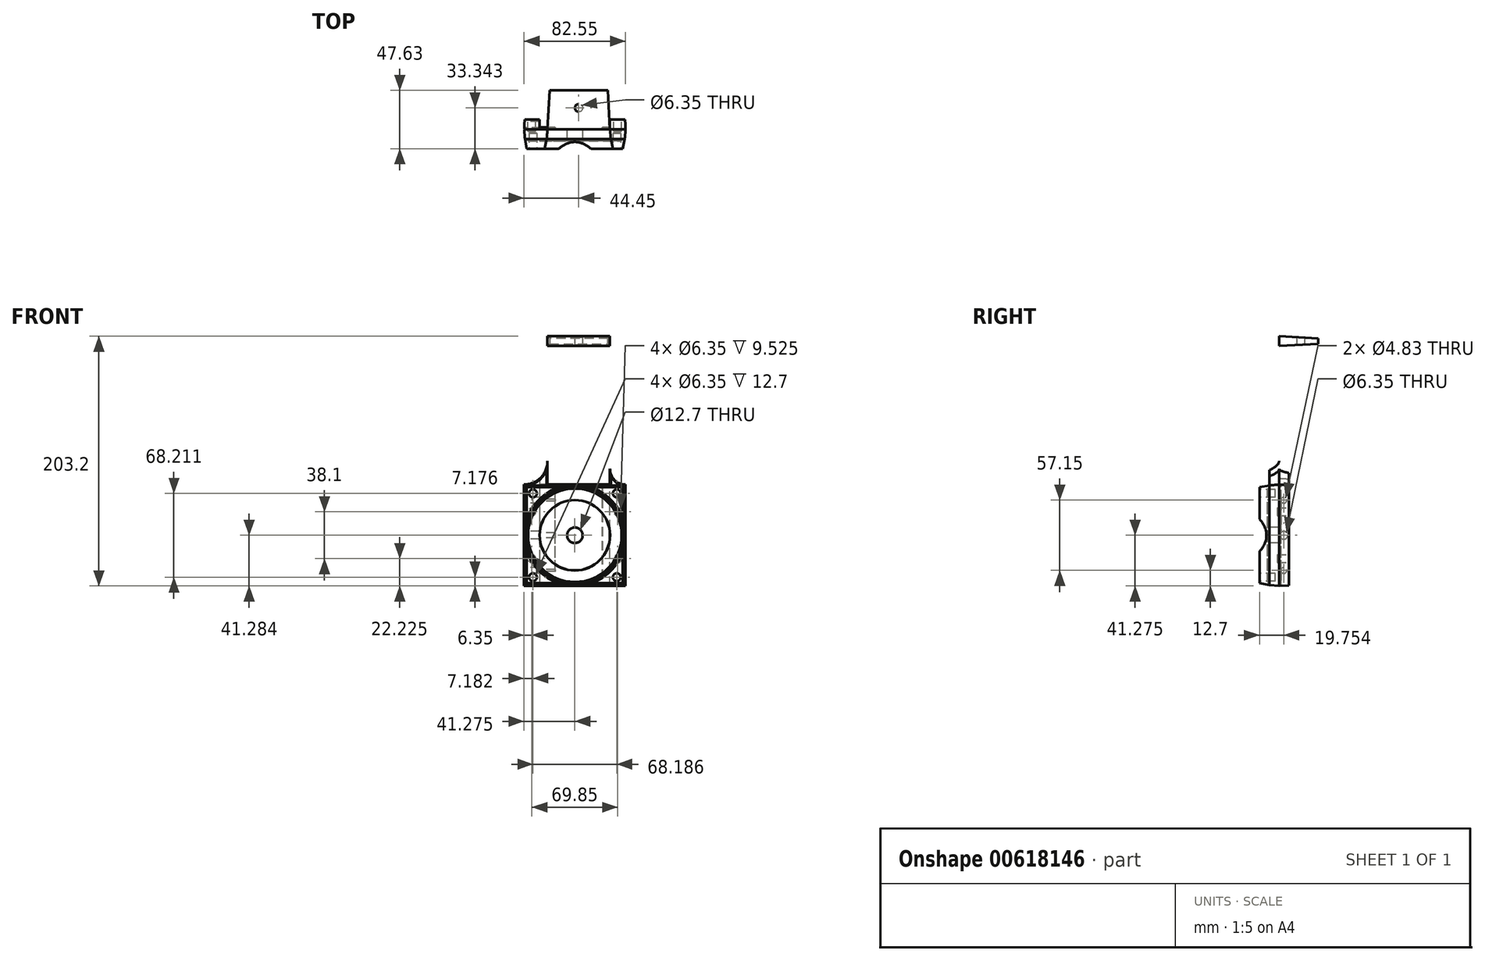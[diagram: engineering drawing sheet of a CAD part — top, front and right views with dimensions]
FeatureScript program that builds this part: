
annotation { "Feature Type Name" : "Feature", "Feature Type Description" : "" }
export const myFeature = defineFeature(function(context is Context, id is Id, definition is map)
    precondition{}
    {
        {
            var Q0;
            Q0=qCreatedBy(makeId("Front.planeOp"),FACE);
            var sketch = newSketch(context, id + "F0", { "sketchPlane" : qUnion([Q0])});
            skLineSegment(sketch, "E0.bottom", {"start": v(0, 0) * mm, "end": v(82.55, 0) * mm});
            skLineSegment(sketch, "E0.top", {"start": v(0, 82.55) * mm, "end": v(82.55, 82.55) * mm});
            skLineSegment(sketch, "E0.left", {"start": v(0, 0) * mm, "end": v(0, 82.55) * mm});
            skLineSegment(sketch, "E0.right", {"start": v(82.55, 0) * mm, "end": v(82.55, 82.55) * mm});
            skLineSegment(sketch, "E1.bottom", {"start": v(19.05, 82.55) * mm, "end": v(69.85, 82.55) * mm});
            skLineSegment(sketch, "E1.top", {"start": v(19.05, 203.2) * mm, "end": v(69.85, 203.2) * mm});
            skLineSegment(sketch, "E1.left", {"start": v(19.05, 82.55) * mm, "end": v(19.05, 203.2) * mm});
            skLineSegment(sketch, "E1.right", {"start": v(69.85, 82.55) * mm, "end": v(69.85, 203.2) * mm});
            skCircle(sketch, "E2", {"center": v(82.55, 95.25) * mm, "radius": 12.7 * mm});
            skCircle(sketch, "E3", {"center": v(0, 101.6) * mm, "radius": 19.05 * mm});
            skSolve(sketch);
        }
        {
            var Q0;
            {var subQ3=sQuery(id+"F0.wireOp",EDGE,"E1.bottom");Q0=makeQuery(id+"F0.imprint","IMPRINT",FACE,{"disambiguationData":[TD([[makeQuery(id+"F0.imprint","IMPRINT",EDGE,{"derivedFrom":subQ3}),1.0]])]});}
            var Q1;
            Q1=makeQuery(id+"F0.imprint","IMPRINT",FACE,{"disambiguationData":[TD([[makeQuery(id+"F0.imprint","IMPRINT",EDGE,{"derivedFrom":sQuery(id+"F0.wireOp",EDGE,"E0.bottom")}),1.0]])]});
            var Q2;
            {var subQ0=sQuery(id+"F0.wireOp",EDGE,"E2");var subQ3=sQuery(id+"F0.wireOp",EDGE,"E1.right");var subQ5=makeQuery(id+"F0.imprint","INTERSECT",VERTEX,{"derivedFrom":[subQ3,subQ0]});Q2=makeQuery(id+"F0.imprint","IMPRINT",FACE,{"disambiguationData":[TD([[makeQuery(id+"F0.imprint","IMPRINT",EDGE,{"disambiguationData":[TD([[subQ5,1.0]])],"derivedFrom":subQ3}),-1.0]])]});}
            var Q3;
            {var subQ0=sQuery(id+"F0.wireOp",EDGE,"E3");var subQ3=sQuery(id+"F0.wireOp",EDGE,"E1.left");var subQ5=makeQuery(id+"F0.imprint","INTERSECT",VERTEX,{"derivedFrom":[subQ3,subQ0]});Q3=makeQuery(id+"F0.imprint","IMPRINT",FACE,{"disambiguationData":[TD([[makeQuery(id+"F0.imprint","IMPRINT",EDGE,{"disambiguationData":[TD([[subQ5,1.0]])],"derivedFrom":subQ3}),1.0]])]});}
            extrude(context, id + "F1", {"entities" : qUnion([Q0, Q1, Q2, Q3]), "depth" : 7.94 * mm, "hasDraft" : true, "draftAngle" : 5 * degree, "draftPullDirection" : true});
        }
        {
            var Q0;
            Q0=makeQuery(id+"F1.opExtrude","CAP_FACE",FACE,{"disambiguationData":[OSD([sQuery(id+"F0.wireOp",EDGE,"E0.bottom"),sQuery(id+"F0.wireOp",EDGE,"E0.top"),sQuery(id+"F0.wireOp",EDGE,"E0.left"),sQuery(id+"F0.wireOp",EDGE,"E0.right"),sQuery(id+"F0.wireOp",EDGE,"E1.top"),sQuery(id+"F0.wireOp",EDGE,"E1.left"),sQuery(id+"F0.wireOp",EDGE,"E1.right")])],"isStart":true});
            var sketch = newSketch(context, id + "F2", { "sketchPlane" : qUnion([Q0])});
            skLineSegment(sketch, "E4.0", {"start": v(-19.05, 203.2) * mm, "end": v(-69.85, 203.2) * mm});
            skLineSegment(sketch, "E5", {"start": v(-69.85, 203.2) * mm, "end": v(-69.85, 195.26) * mm});
            skLineSegment(sketch, "E6", {"start": v(-69.85, 195.26) * mm, "end": v(-19.05, 195.26) * mm});
            skLineSegment(sketch, "E7", {"start": v(-19.05, 195.26) * mm, "end": v(-19.05, 203.2) * mm});
            skSolve(sketch);
        }
        {
            var Q0;
            Q0=makeQuery(id+"F2.imprint","IMPRINT",FACE,{"disambiguationData":[TD([[makeQuery(id+"F2.imprint","IMPRINT",EDGE,{"derivedFrom":sQuery(id+"F2.wireOp",EDGE,"E4.0")}),1.0]])]});
            extrude(context, id + "F3", {"entities" : qUnion([Q0]), "operationType" : NewBodyOperationType.ADD, "depth" : 31.75 * mm, "hasDraft" : true, "draftAngle" : 3 * degree, "draftPullDirection" : true});
        }
        {
            var Q0;
            Q0=makeQuery(id+"F1.opExtrude","CAP_FACE",FACE,{"disambiguationData":[OSD([sQuery(id+"F0.wireOp",EDGE,"E0.bottom"),sQuery(id+"F0.wireOp",EDGE,"E0.left"),sQuery(id+"F0.wireOp",EDGE,"E0.right"),sQuery(id+"F0.wireOp",EDGE,"E1.top"),sQuery(id+"F0.wireOp",EDGE,"E1.left"),sQuery(id+"F0.wireOp",EDGE,"E1.right"),sQuery(id+"F0.wireOp",EDGE,"E2"),sQuery(id+"F0.wireOp",EDGE,"E3")])],"isStart":true});
            var sketch = newSketch(context, id + "F4", { "sketchPlane" : qUnion([Q0])});
            skLineSegment(sketch, "E8.bottom", {"start": v(-82.55, 82.55) * mm, "end": v(-69.85, 82.55) * mm});
            skLineSegment(sketch, "E8.top", {"start": v(-82.55, 0) * mm, "end": v(-69.85, 0) * mm});
            skLineSegment(sketch, "E8.left", {"start": v(-82.55, 82.55) * mm, "end": v(-82.55, 0) * mm});
            skLineSegment(sketch, "E8.right", {"start": v(-69.85, 95.25) * mm, "end": v(-69.85, 0) * mm});
            skLineSegment(sketch, "E9.bottom", {"start": v(0, 82.55) * mm, "end": v(-12.7, 82.55) * mm});
            skLineSegment(sketch, "E9.top", {"start": v(0, 0) * mm, "end": v(-12.7, 0) * mm});
            skLineSegment(sketch, "E9.left", {"start": v(0, 82.55) * mm, "end": v(0, 0) * mm});
            skLineSegment(sketch, "E9.right", {"start": v(-12.7, 87.4) * mm, "end": v(-12.7, 0) * mm});
            skArc(sketch, "E10.0", {"start": v(-69.85, 95.25) * mm, "mid": v(-73.57, 86.27) * mm, "end": v(-82.55, 82.55) * mm});
            skArc(sketch, "E11.0", {"start": v(0, 82.55) * mm, "mid": v(-13.47, 88.13) * mm, "end": v(-19.05, 101.6) * mm});
            skSolve(sketch);
        }
        {
            var Q0;
            Q0=qSketchRegion(id+"F4",true);
            extrude(context, id + "F5", {"entities" : qUnion([Q0]), "operationType" : NewBodyOperationType.ADD, "depth" : 7.94 * mm});
        }
        {
            var Q0;
            Q0=makeQuery(id+"F1.opExtrude","CAP_FACE",FACE,{"disambiguationData":[OSD([sQuery(id+"F0.wireOp",EDGE,"E0.bottom"),sQuery(id+"F0.wireOp",EDGE,"E0.left"),sQuery(id+"F0.wireOp",EDGE,"E0.right"),sQuery(id+"F0.wireOp",EDGE,"E1.top"),sQuery(id+"F0.wireOp",EDGE,"E1.left"),sQuery(id+"F0.wireOp",EDGE,"E1.right"),sQuery(id+"F0.wireOp",EDGE,"E2"),sQuery(id+"F0.wireOp",EDGE,"E3")])],"isStart":true});
            var sketch = newSketch(context, id + "F6", { "sketchPlane" : qUnion([Q0])});
            skLineSegment(sketch, "E12.0.0", {"start": v(-12.7, 0) * mm, "end": v(-12.7, 87.4) * mm});
            skArc(sketch, "E12.0.1", {"start": v(-12.7, 87.4) * mm, "mid": v(-17.4, 93.82) * mm, "end": v(-19.05, 101.6) * mm});
            skLineSegment(sketch, "E12.0.2", {"start": v(-19.05, 101.6) * mm, "end": v(-19.05, 195.26) * mm});
            skLineSegment(sketch, "E12.0.3", {"start": v(-69.85, 195.26) * mm, "end": v(-19.05, 195.26) * mm});
            skLineSegment(sketch, "E12.0.4", {"start": v(-69.85, 95.25) * mm, "end": v(-69.85, 195.26) * mm});
            skLineSegment(sketch, "E12.0.5", {"start": v(-69.85, 95.25) * mm, "end": v(-69.85, 0) * mm});
            skLineSegment(sketch, "E12.0.6", {"start": v(-12.7, 0) * mm, "end": v(-69.85, 0) * mm});
            skLineSegment(sketch, "E13.0.0", {"start": v(0, 0) * mm, "end": v(0, 82.55) * mm});
            skArc(sketch, "E13.0.1", {"start": v(0, 82.55) * mm, "mid": v(-6.8, 83.8) * mm, "end": v(-12.7, 87.4) * mm});
            skLineSegment(sketch, "E13.0.2", {"start": v(-12.7, 87.4) * mm, "end": v(-12.7, 0) * mm});
            skLineSegment(sketch, "E13.0.3", {"start": v(0, 0) * mm, "end": v(-12.7, 0) * mm});
            skLineSegment(sketch, "E14.0.0", {"start": v(-69.85, 0) * mm, "end": v(-69.85, 95.25) * mm});
            skArc(sketch, "E14.0.1", {"start": v(-69.85, 95.25) * mm, "mid": v(-73.57, 86.27) * mm, "end": v(-82.55, 82.55) * mm});
            skLineSegment(sketch, "E14.0.2", {"start": v(-82.55, 0) * mm, "end": v(-82.55, 82.55) * mm});
            skLineSegment(sketch, "E14.0.3", {"start": v(-69.85, 0) * mm, "end": v(-82.55, 0) * mm});
            skLineSegment(sketch, "E15.0", {"start": v(-19.05, 195.26) * mm, "end": v(-19.05, 203.2) * mm});
            skLineSegment(sketch, "E16.0", {"start": v(-19.05, 203.2) * mm, "end": v(-69.85, 203.2) * mm});
            skLineSegment(sketch, "E17.0", {"start": v(-69.85, 195.26) * mm, "end": v(-69.85, 203.2) * mm});
            skCircle(sketch, "E18", {"center": v(-82.55, 0) * mm, "radius": 254 * mm});
            skSolve(sketch);
        }
        {
            var Q0;
            Q0=qSketchRegion(id+"F6",true);
            extrude(context, id + "F7", {"entities" : qUnion([Q0]), "operationType" : NewBodyOperationType.REMOVE, "depth" : 25.4 * mm, "hasDraft" : true, "draftAngle" : 3 * degree});
        }
        {
            var Q0;
            Q0=makeQuery(id+"F1.opExtrude","CAP_FACE",FACE,{"disambiguationData":[OSD([sQuery(id+"F0.wireOp",EDGE,"E0.bottom"),sQuery(id+"F0.wireOp",EDGE,"E0.left"),sQuery(id+"F0.wireOp",EDGE,"E0.right"),sQuery(id+"F0.wireOp",EDGE,"E1.top"),sQuery(id+"F0.wireOp",EDGE,"E1.left"),sQuery(id+"F0.wireOp",EDGE,"E1.right"),sQuery(id+"F0.wireOp",EDGE,"E2"),sQuery(id+"F0.wireOp",EDGE,"E3")])],"isStart":true});
            var sketch = newSketch(context, id + "F8", { "sketchPlane" : qUnion([Q0])});
            skLineSegment(sketch, "E19.0", {"start": v(0, 0) * mm, "end": v(0, 82.55) * mm});
            skLineSegment(sketch, "E20.0", {"start": v(-82.55, 0) * mm, "end": v(-82.55, 82.55) * mm});
            skLineSegment(sketch, "E21.0", {"start": v(-12.7, 0) * mm, "end": v(-69.85, 0) * mm});
            skLineSegment(sketch, "E22.bottom", {"start": v(0, 82.55) * mm, "end": v(-25.4, 82.55) * mm});
            skLineSegment(sketch, "E22.top", {"start": v(0, 0) * mm, "end": v(-25.4, 0) * mm});
            skLineSegment(sketch, "E22.left", {"start": v(0, 82.55) * mm, "end": v(0, 0) * mm});
            skLineSegment(sketch, "E22.right", {"start": v(-25.4, 82.55) * mm, "end": v(-25.4, 0) * mm});
            skLineSegment(sketch, "E23.bottom", {"start": v(-82.55, 82.55) * mm, "end": v(-63.5, 82.55) * mm});
            skLineSegment(sketch, "E23.top", {"start": v(-82.55, 0) * mm, "end": v(-63.5, 0) * mm});
            skLineSegment(sketch, "E23.left", {"start": v(-82.55, 82.55) * mm, "end": v(-82.55, 0) * mm});
            skLineSegment(sketch, "E23.right", {"start": v(-63.5, 82.55) * mm, "end": v(-63.5, 0) * mm});
            skSolve(sketch);
        }
        {
            var Q0;
            Q0=qSketchRegion(id+"F8",true);
            extrude(context, id + "F9", {"entities" : qUnion([Q0]), "operationType" : NewBodyOperationType.ADD, "depth" : 1.59 * mm, "hasDraft" : true, "draftAngle" : 3 * degree, "draftPullDirection" : true});
        }
        {
            var Q0;
            Q0=makeQuery(id+"F1.opExtrude","CAP_FACE",FACE,{"disambiguationData":[OSD([sQuery(id+"F0.wireOp",EDGE,"E0.bottom"),sQuery(id+"F0.wireOp",EDGE,"E0.left"),sQuery(id+"F0.wireOp",EDGE,"E0.right"),sQuery(id+"F0.wireOp",EDGE,"E1.top"),sQuery(id+"F0.wireOp",EDGE,"E1.left"),sQuery(id+"F0.wireOp",EDGE,"E1.right"),sQuery(id+"F0.wireOp",EDGE,"E2"),sQuery(id+"F0.wireOp",EDGE,"E3")])],"isStart":false});
            var sketch = newSketch(context, id + "F10", { "sketchPlane" : qUnion([Q0])});
            skLineSegment(sketch, "E24", {"start": v(0.7, 0.7) * mm, "end": v(81.86, 81.87) * mm, "construction": true});
            skCircle(sketch, "E25", {"center": v(41.28, 41.28) * mm, "radius": 6.35 * mm});
            skSolve(sketch);
        }
        {
            var Q0;
            Q0=qSketchRegion(id+"F10",true);
            extrude(context, id + "F11", {"entities" : qUnion([Q0]), "operationType" : NewBodyOperationType.REMOVE, "endBound" : BoundingType.THROUGH_ALL, "oppositeDirection" : true, "depth" : 25.4 * mm});
        }
        {
            var Q0;
            Q0=makeQuery(id+"F1.opExtrude","CAP_FACE",FACE,{"disambiguationData":[OSD([sQuery(id+"F0.wireOp",EDGE,"E0.bottom"),sQuery(id+"F0.wireOp",EDGE,"E0.left"),sQuery(id+"F0.wireOp",EDGE,"E0.right"),sQuery(id+"F0.wireOp",EDGE,"E1.top"),sQuery(id+"F0.wireOp",EDGE,"E1.left"),sQuery(id+"F0.wireOp",EDGE,"E1.right"),sQuery(id+"F0.wireOp",EDGE,"E2"),sQuery(id+"F0.wireOp",EDGE,"E3")])],"isStart":false});
            var sketch = newSketch(context, id + "F12", { "sketchPlane" : qUnion([Q0])});
            skCircle(sketch, "E26", {"center": v(41.28, 41.28) * mm, "radius": 28.58 * mm});
            skCircle(sketch, "E27", {"center": v(41.28, 41.28) * mm, "radius": 38.1 * mm});
            skSolve(sketch);
        }
        {
            var Q0;
            Q0=qSketchRegion(id+"F12",true);
            extrude(context, id + "F13", {"entities" : qUnion([Q0]), "operationType" : NewBodyOperationType.ADD, "depth" : 1.59 * mm, "hasDraft" : true, "draftAngle" : 3 * degree, "draftPullDirection" : true});
        }
        {
            var Q0;
            {var subQ0=sQuery(id+"F0.wireOp",EDGE,"E0.right");var subQ1=sQuery(id+"F0.wireOp",EDGE,"E0.left");var subQ2=sQuery(id+"F0.wireOp",EDGE,"E1.top");var subQ3=sQuery(id+"F0.wireOp",EDGE,"E0.bottom");var subQ4=sQuery(id+"F0.wireOp",EDGE,"E1.left");var subQ5=sQuery(id+"F0.wireOp",EDGE,"E1.right");var subQ6=sQuery(id+"F0.wireOp",EDGE,"E2");var subQ7=sQuery(id+"F0.wireOp",EDGE,"E3");Q0=makeQuery(id+"F13.boolean.opBoolean","SPLIT",FACE,{"disambiguationData":[TD([makeQuery(id+"F1.opExtrude","SWEPT_FACE",FACE,{"disambiguationData":[OSD([subQ3])]})])],"derivedFrom":makeQuery(id+"F1.opExtrude","CAP_FACE",FACE,{"disambiguationData":[OSD([subQ3,subQ1,subQ0,subQ2,subQ4,subQ5,subQ6,subQ7])],"isStart":false})});}
            var sketch = newSketch(context, id + "F14", { "sketchPlane" : qUnion([Q0])});
            skLineSegment(sketch, "E28.0.2", {"start": v(0.7, 81.87) * mm, "end": v(0.7, 0.7) * mm});
            skLineSegment(sketch, "E28.0.3", {"start": v(0.7, 0.7) * mm, "end": v(81.86, 0.7) * mm});
            skLineSegment(sketch, "E28.0.4", {"start": v(81.86, 0.7) * mm, "end": v(81.86, 81.87) * mm});
            skLineSegment(sketch, "E29", {"start": v(0.7, 81.87) * mm, "end": v(81.86, 81.87) * mm});
            skCircle(sketch, "E30", {"center": v(41.28, 41.28) * mm, "radius": 39.69 * mm});
            skLineSegment(sketch, "E31", {"start": v(41.28, 41.28) * mm, "end": v(49.21, 41.28) * mm, "construction": true});
            skLineSegment(sketch, "E32", {"start": v(49.21, 41.28) * mm, "end": v(49.21, 42.87) * mm, "construction": true});
            skLineSegment(sketch, "E33", {"start": v(49.21, 42.87) * mm, "end": v(41.28, 41.28) * mm, "construction": true});
            skSolve(sketch);
        }
        {
            var Q0;
            Q0=makeQuery(id+"F14.imprint","IMPRINT",FACE,{"disambiguationData":[TD([[makeQuery(id+"F14.imprint","IMPRINT",EDGE,{"derivedFrom":sQuery(id+"F14.wireOp",EDGE,"E28.0.2")}),-1.0]])]});
            extrude(context, id + "F15", {"entities" : qUnion([Q0]), "operationType" : NewBodyOperationType.ADD, "depth" : 7.94 * mm, "hasDraft" : true, "draftAngle" : 11 * degree, "draftPullDirection" : true});
        }
        {
            var Q0;
            Q0=makeQuery(id+"F5.opExtrude","CAP_FACE",FACE,{"disambiguationData":[OSD([sQuery(id+"F4.wireOp",EDGE,"E8.top"),sQuery(id+"F4.wireOp",EDGE,"E8.left"),sQuery(id+"F4.wireOp",EDGE,"E8.right"),sQuery(id+"F4.wireOp",EDGE,"E10.0")])],"isStart":false});
            var sketch = newSketch(context, id + "F16", { "sketchPlane" : qUnion([Q0])});
            skCircle(sketch, "E34", {"center": v(-76.2, 22.23) * mm, "radius": 3.18 * mm});
            skCircle(sketch, "E35", {"center": v(-76.2, 60.32) * mm, "radius": 3.18 * mm});
            skCircle(sketch, "E36", {"center": v(-6.35, 60.32) * mm, "radius": 3.18 * mm});
            skCircle(sketch, "E37", {"center": v(-6.35, 22.23) * mm, "radius": 3.18 * mm});
            skSolve(sketch);
        }
        {
            var Q0;
            Q0=qSketchRegion(id+"F16",true);
            extrude(context, id + "F17", {"entities" : qUnion([Q0]), "operationType" : NewBodyOperationType.REMOVE, "oppositeDirection" : true, "depth" : 9.52 * mm});
        }
        {
            var Q0;
            Q0=qCreatedBy(makeId("Right.planeOp"),FACE);
            var sketch = newSketch(context, id + "F18", { "sketchPlane" : qUnion([Q0])});
            skLineSegment(sketch, "E38.0", {"start": v(0, 82.55) * mm, "end": v(0, 0) * mm, "construction": true});
            skLineSegment(sketch, "E39.0", {"start": v(7.94, 86.85) * mm, "end": v(7.94, 0.42) * mm, "construction": true});
            skCircle(sketch, "E40", {"center": v(3.87, 69.85) * mm, "radius": 2.41 * mm});
            skCircle(sketch, "E41", {"center": v(3.87, 12.7) * mm, "radius": 2.41 * mm});
            skLineSegment(sketch, "E42", {"start": v(0, 41.28) * mm, "end": v(7.94, 41.28) * mm, "construction": true});
            skCircle(sketch, "E43", {"center": v(3.87, 41.28) * mm, "radius": 3.18 * mm});
            skSolve(sketch);
        }
        {
            var Q0;
            Q0=qSketchRegion(id+"F18",true);
            extrude(context, id + "F19", {"entities" : qUnion([Q0]), "operationType" : NewBodyOperationType.REMOVE, "depth" : 25.4 * mm});
        }
        {
            var Q0;
            Q0=qCreatedBy(makeId("Top.planeOp"),FACE);
            var sketch = newSketch(context, id + "F20", { "sketchPlane" : qUnion([Q0])});
            skLineSegment(sketch, "E44.0.0", {"start": v(69.85, 0) * mm, "end": v(19.05, 0) * mm});
            skLineSegment(sketch, "E44.0.1", {"start": v(19.05, 0) * mm, "end": v(20.71, 31.75) * mm});
            skLineSegment(sketch, "E44.0.2", {"start": v(68.19, 31.75) * mm, "end": v(20.71, 31.75) * mm});
            skLineSegment(sketch, "E44.0.3", {"start": v(68.19, 31.75) * mm, "end": v(69.85, 0) * mm});
            skLineSegment(sketch, "E45", {"start": v(44.45, 31.75) * mm, "end": v(44.45, 0) * mm});
            skCircle(sketch, "E46", {"center": v(44.45, 17.46) * mm, "radius": 3.18 * mm});
            skSolve(sketch);
        }
        {
            var Q0;
            {var subQ0=sQuery(id+"F20.wireOp",EDGE,"E46");var subQ1=sQuery(id+"F20.wireOp",EDGE,"E45");var subQ2=makeQuery(id+"F20.imprint","INTERSECT",VERTEX,{"disambiguationData":[OD(0.0)],"derivedFrom":[subQ1,subQ0]});Q0=makeQuery(id+"F20.imprint","IMPRINT",FACE,{"disambiguationData":[TD([[makeQuery(id+"F20.imprint","IMPRINT",EDGE,{"disambiguationData":[TD([[subQ2,-1.0]])],"derivedFrom":subQ1}),1.0]])]});}
            var Q1;
            {var subQ0=sQuery(id+"F20.wireOp",EDGE,"E46");var subQ1=sQuery(id+"F20.wireOp",EDGE,"E45");var subQ2=makeQuery(id+"F20.imprint","INTERSECT",VERTEX,{"disambiguationData":[OD(0.0)],"derivedFrom":[subQ1,subQ0]});Q1=makeQuery(id+"F20.imprint","IMPRINT",FACE,{"disambiguationData":[TD([[makeQuery(id+"F20.imprint","IMPRINT",EDGE,{"disambiguationData":[TD([[subQ2,-1.0]])],"derivedFrom":subQ1}),-1.0]])]});}
            extrude(context, id + "F21", {"entities" : qUnion([Q0, Q1]), "operationType" : NewBodyOperationType.REMOVE, "endBound" : BoundingType.THROUGH_ALL, "depth" : 25.4 * mm});
        }
        {
            var Q0;
            Q0=makeQuery(id+"F15.*.draft.opDraft","SPLIT",FACE,{"disambiguationData":[OD(2.0)],"derivedFrom":makeQuery(id+"F15.opExtrude","CAP_FACE",FACE,{"disambiguationData":[OSD([sQuery(id+"F14.wireOp",EDGE,"E28.0.2"),sQuery(id+"F14.wireOp",EDGE,"E28.0.3"),sQuery(id+"F14.wireOp",EDGE,"E28.0.4"),sQuery(id+"F14.wireOp",EDGE,"E29"),sQuery(id+"F14.wireOp",EDGE,"E30")])],"isStart":false})});
            var sketch = newSketch(context, id + "F22", { "sketchPlane" : qUnion([Q0])});
            skLineSegment(sketch, "E47.0.0", {"start": v(2.24, 80.32) * mm, "end": v(2.24, 54.55) * mm});
            skArc(sketch, "E47.0.1", {"start": v(2.24, 54.55) * mm, "mid": v(12.13, 70.44) * mm, "end": v(28.02, 80.33) * mm});
            skLineSegment(sketch, "E47.0.2", {"start": v(28.02, 80.33) * mm, "end": v(2.24, 80.32) * mm});
            skLineSegment(sketch, "E48.0.0", {"start": v(80.31, 80.33) * mm, "end": v(54.52, 80.33) * mm});
            skArc(sketch, "E48.0.1", {"start": v(54.52, 80.33) * mm, "mid": v(70.42, 70.45) * mm, "end": v(80.31, 54.55) * mm});
            skLineSegment(sketch, "E48.0.2", {"start": v(80.31, 54.55) * mm, "end": v(80.31, 80.33) * mm});
            skLineSegment(sketch, "E49.0.0", {"start": v(80.31, 2.24) * mm, "end": v(80.31, 28.02) * mm});
            skArc(sketch, "E49.0.1", {"start": v(80.31, 28.02) * mm, "mid": v(70.42, 12.12) * mm, "end": v(54.52, 2.24) * mm});
            skLineSegment(sketch, "E49.0.2", {"start": v(54.52, 2.24) * mm, "end": v(80.31, 2.24) * mm});
            skLineSegment(sketch, "E50.0.0", {"start": v(2.24, 2.24) * mm, "end": v(28.03, 2.24) * mm});
            skArc(sketch, "E50.0.1", {"start": v(28.03, 2.24) * mm, "mid": v(12.13, 12.12) * mm, "end": v(2.24, 28.02) * mm});
            skLineSegment(sketch, "E50.0.2", {"start": v(2.24, 28.02) * mm, "end": v(2.24, 2.24) * mm});
            skLineSegment(sketch, "E51", {"start": v(2.24, 80.32) * mm, "end": v(12.13, 70.44) * mm});
            skLineSegment(sketch, "E52", {"start": v(12.13, 70.44) * mm, "end": v(70.42, 70.44) * mm});
            skLineSegment(sketch, "E53", {"start": v(70.42, 70.44) * mm, "end": v(80.31, 80.33) * mm});
            skLineSegment(sketch, "E54", {"start": v(80.31, 2.24) * mm, "end": v(70.42, 12.12) * mm});
            skLineSegment(sketch, "E55", {"start": v(70.42, 12.12) * mm, "end": v(12.13, 12.12) * mm});
            skLineSegment(sketch, "E56", {"start": v(12.13, 12.12) * mm, "end": v(2.24, 2.24) * mm});
            skCircle(sketch, "E57", {"center": v(7.18, 75.38) * mm, "radius": 3.18 * mm});
            skCircle(sketch, "E58", {"center": v(75.37, 75.39) * mm, "radius": 3.18 * mm});
            skCircle(sketch, "E59", {"center": v(75.37, 7.18) * mm, "radius": 3.18 * mm});
            skCircle(sketch, "E60", {"center": v(7.19, 7.18) * mm, "radius": 3.18 * mm});
            skSolve(sketch);
        }
        {
            var Q0;
            {var subQ0=sQuery(id+"F22.wireOp",EDGE,"E57");var subQ1=sQuery(id+"F22.wireOp",EDGE,"E51");var subQ2=makeQuery(id+"F22.imprint","INTERSECT",VERTEX,{"disambiguationData":[OD(0.0)],"derivedFrom":[subQ1,subQ0]});Q0=makeQuery(id+"F22.imprint","IMPRINT",FACE,{"disambiguationData":[TD([[makeQuery(id+"F22.imprint","IMPRINT",EDGE,{"disambiguationData":[TD([[subQ2,-1.0]])],"derivedFrom":subQ1}),1.0]])]});}
            var Q1;
            {var subQ0=sQuery(id+"F22.wireOp",EDGE,"E57");var subQ1=sQuery(id+"F22.wireOp",EDGE,"E51");var subQ2=makeQuery(id+"F22.imprint","INTERSECT",VERTEX,{"disambiguationData":[OD(0.0)],"derivedFrom":[subQ1,subQ0]});Q1=makeQuery(id+"F22.imprint","IMPRINT",FACE,{"disambiguationData":[TD([[makeQuery(id+"F22.imprint","IMPRINT",EDGE,{"disambiguationData":[TD([[subQ2,-1.0]])],"derivedFrom":subQ1}),-1.0]])]});}
            var Q2;
            {var subQ0=sQuery(id+"F22.wireOp",EDGE,"E58");var subQ1=sQuery(id+"F22.wireOp",EDGE,"E53");var subQ2=makeQuery(id+"F22.imprint","INTERSECT",VERTEX,{"disambiguationData":[OD(0.0)],"derivedFrom":[subQ1,subQ0]});Q2=makeQuery(id+"F22.imprint","IMPRINT",FACE,{"disambiguationData":[TD([[makeQuery(id+"F22.imprint","IMPRINT",EDGE,{"disambiguationData":[TD([[subQ2,-1.0]])],"derivedFrom":subQ1}),1.0]])]});}
            var Q3;
            {var subQ0=sQuery(id+"F22.wireOp",EDGE,"E58");var subQ1=sQuery(id+"F22.wireOp",EDGE,"E53");var subQ2=makeQuery(id+"F22.imprint","INTERSECT",VERTEX,{"disambiguationData":[OD(0.0)],"derivedFrom":[subQ1,subQ0]});Q3=makeQuery(id+"F22.imprint","IMPRINT",FACE,{"disambiguationData":[TD([[makeQuery(id+"F22.imprint","IMPRINT",EDGE,{"disambiguationData":[TD([[subQ2,-1.0]])],"derivedFrom":subQ1}),-1.0]])]});}
            var Q4;
            {var subQ0=sQuery(id+"F22.wireOp",EDGE,"E59");var subQ1=sQuery(id+"F22.wireOp",EDGE,"E54");var subQ2=makeQuery(id+"F22.imprint","INTERSECT",VERTEX,{"disambiguationData":[OD(0.0)],"derivedFrom":[subQ1,subQ0]});Q4=makeQuery(id+"F22.imprint","IMPRINT",FACE,{"disambiguationData":[TD([[makeQuery(id+"F22.imprint","IMPRINT",EDGE,{"disambiguationData":[TD([[subQ2,-1.0]])],"derivedFrom":subQ1}),-1.0]])]});}
            var Q5;
            {var subQ0=sQuery(id+"F22.wireOp",EDGE,"E59");var subQ1=sQuery(id+"F22.wireOp",EDGE,"E54");var subQ2=makeQuery(id+"F22.imprint","INTERSECT",VERTEX,{"disambiguationData":[OD(0.0)],"derivedFrom":[subQ1,subQ0]});Q5=makeQuery(id+"F22.imprint","IMPRINT",FACE,{"disambiguationData":[TD([[makeQuery(id+"F22.imprint","IMPRINT",EDGE,{"disambiguationData":[TD([[subQ2,-1.0]])],"derivedFrom":subQ1}),1.0]])]});}
            var Q6;
            {var subQ0=sQuery(id+"F22.wireOp",EDGE,"E60");var subQ1=sQuery(id+"F22.wireOp",EDGE,"E56");var subQ2=makeQuery(id+"F22.imprint","INTERSECT",VERTEX,{"disambiguationData":[OD(0.0)],"derivedFrom":[subQ1,subQ0]});Q6=makeQuery(id+"F22.imprint","IMPRINT",FACE,{"disambiguationData":[TD([[makeQuery(id+"F22.imprint","IMPRINT",EDGE,{"disambiguationData":[TD([[subQ2,-1.0]])],"derivedFrom":subQ1}),-1.0]])]});}
            var Q7;
            {var subQ0=sQuery(id+"F22.wireOp",EDGE,"E60");var subQ1=sQuery(id+"F22.wireOp",EDGE,"E56");var subQ2=makeQuery(id+"F22.imprint","INTERSECT",VERTEX,{"disambiguationData":[OD(0.0)],"derivedFrom":[subQ1,subQ0]});Q7=makeQuery(id+"F22.imprint","IMPRINT",FACE,{"disambiguationData":[TD([[makeQuery(id+"F22.imprint","IMPRINT",EDGE,{"disambiguationData":[TD([[subQ2,-1.0]])],"derivedFrom":subQ1}),1.0]])]});}
            extrude(context, id + "F23", {"entities" : qUnion([Q0, Q1, Q2, Q3, Q4, Q5, Q6, Q7]), "operationType" : NewBodyOperationType.REMOVE, "oppositeDirection" : true, "depth" : 12.7 * mm});
        }
    });
